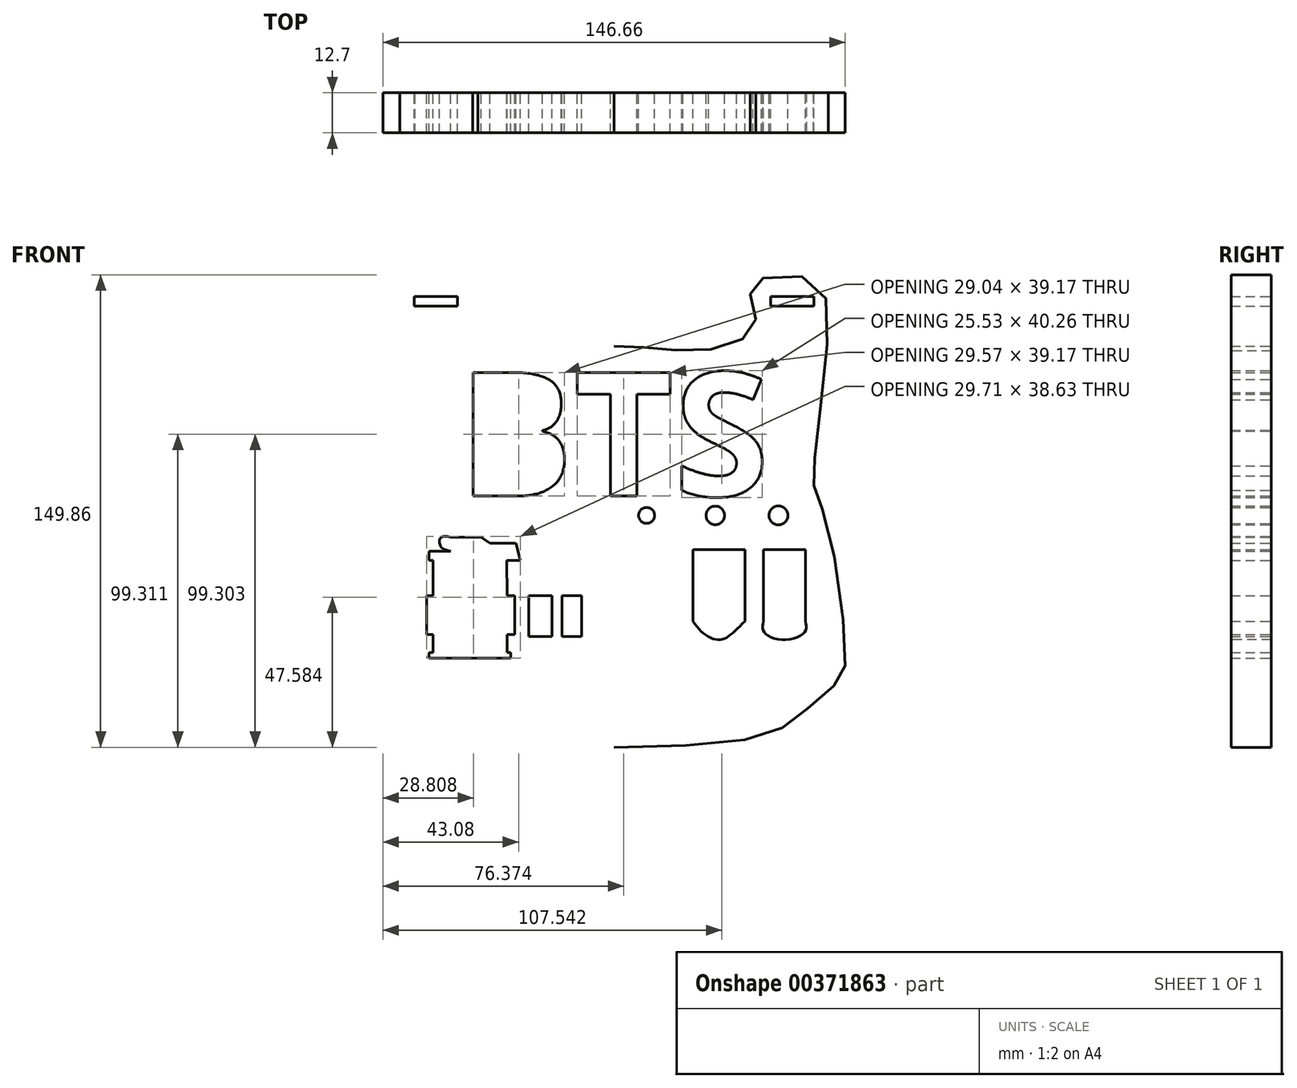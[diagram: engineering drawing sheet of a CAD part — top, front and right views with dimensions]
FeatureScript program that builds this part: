
annotation { "Feature Type Name" : "Feature", "Feature Type Description" : "" }
export const myFeature = defineFeature(function(context is Context, id is Id, definition is map)
    precondition{}
    {
        {
            var Q0;
            Q0=qCreatedBy(makeId("Front.planeOp"),FACE);
            var sketch = newSketch(context, id + "F0", { "sketchPlane" : qUnion([Q0])});
            skFitSpline(sketch, "E0", {"points": [v(0, 47.49) * mm, v(-11.8, 46.91) * mm, v(-26.2, 46.05) * mm, v(-40.87, 49.8) * mm, v(-44.9, 55.83) * mm, v(-43.17, 64.18) * mm, v(-45.76, 68.5) * mm, v(-63.32, 68.2) * mm, v(-67.63, 48.93) * mm, v(-63.32, 9.2) * mm, v(-63.6, 2.3) * mm, v(-67.92, -10.07) * mm, v(-73.32, -52.11) * mm, v(-70.96, -58.89) * mm, v(-59.95, -68.62) * mm, v(-48.35, -75.7) * mm, v(0, -79.72) * mm], "startDerivative": vector(-215.17, -5.96) * mm, "endDerivative": vector(548.69, -6.84) * mm});
            skFitSpline(sketch, "E1.MirrorCS", {"points": [v(0, 47.49) * mm, v(11.8, 46.91) * mm, v(26.2, 46.05) * mm, v(40.87, 49.8) * mm, v(44.9, 55.83) * mm, v(43.17, 64.18) * mm, v(45.76, 68.5) * mm, v(63.32, 68.2) * mm, v(67.63, 48.93) * mm, v(63.32, 9.2) * mm, v(63.6, 2.3) * mm, v(67.92, -10.07) * mm, v(73.32, -52.11) * mm, v(70.96, -58.89) * mm, v(59.95, -68.62) * mm, v(48.35, -75.7) * mm, v(0, -79.72) * mm], "startDerivative": vector(215.17, -5.96) * mm, "endDerivative": vector(-548.69, -6.84) * mm});
            skLineSegment(sketch, "E2", {"start": v(-58.71, -17.56) * mm, "end": v(-58.71, -20.44) * mm});
            skLineSegment(sketch, "E3", {"start": v(-58.71, -20.44) * mm, "end": v(-32.8, -20.44) * mm});
            skLineSegment(sketch, "E4", {"start": v(-32.8, -20.44) * mm, "end": v(-32.8, -17.56) * mm});
            skLineSegment(sketch, "E5", {"start": v(-32.8, -17.56) * mm, "end": v(-58.71, -17.56) * mm});
            skLineSegment(sketch, "E6", {"start": v(-57.44, -20.44) * mm, "end": v(-57.44, -31.6) * mm});
            skLineSegment(sketch, "E7", {"start": v(-57.44, -31.6) * mm, "end": v(-33.87, -31.6) * mm});
            skLineSegment(sketch, "E8", {"start": v(-34.07, -20.44) * mm, "end": v(-33.87, -31.6) * mm});
            skLineSegment(sketch, "E9", {"start": v(-57.44, -31.6) * mm, "end": v(-59.38, -31.6) * mm});
            skLineSegment(sketch, "E10", {"start": v(-59.38, -31.6) * mm, "end": v(-59.38, -44) * mm});
            skLineSegment(sketch, "E11", {"start": v(-59.38, -44) * mm, "end": v(-31.55, -44) * mm});
            skLineSegment(sketch, "E12", {"start": v(-31.55, -44) * mm, "end": v(-31.55, -31.6) * mm});
            skLineSegment(sketch, "E13", {"start": v(-31.55, -31.6) * mm, "end": v(-33.87, -31.6) * mm});
            skLineSegment(sketch, "E14", {"start": v(-57.44, -44) * mm, "end": v(-57.44, -49.66) * mm});
            skLineSegment(sketch, "E15", {"start": v(-57.44, -49.66) * mm, "end": v(-33.87, -49.66) * mm});
            skLineSegment(sketch, "E16", {"start": v(-33.87, -49.66) * mm, "end": v(-33.87, -44) * mm});
            skLineSegment(sketch, "E17", {"start": v(-57.44, -49.66) * mm, "end": v(-58.71, -49.66) * mm});
            skLineSegment(sketch, "E18", {"start": v(-58.71, -49.66) * mm, "end": v(-58.71, -51.45) * mm});
            skLineSegment(sketch, "E19", {"start": v(-58.71, -51.45) * mm, "end": v(-32.8, -51.45) * mm});
            skLineSegment(sketch, "E20", {"start": v(-32.8, -51.45) * mm, "end": v(-32.8, -49.66) * mm});
            skLineSegment(sketch, "E21", {"start": v(-32.8, -49.66) * mm, "end": v(-33.87, -49.66) * mm});
            skLineSegment(sketch, "E22", {"start": v(-51.85, -17.56) * mm, "end": v(-51.85, -13.04) * mm});
            skLineSegment(sketch, "E23", {"start": v(-51.85, -13.04) * mm, "end": v(-42.16, -13.04) * mm});
            skLineSegment(sketch, "E24", {"start": v(-42.16, -13.04) * mm, "end": v(-39.36, -15) * mm});
            skLineSegment(sketch, "E25", {"start": v(-39.36, -15) * mm, "end": v(-31.14, -15) * mm});
            skLineSegment(sketch, "E26", {"start": v(-31.14, -15) * mm, "end": v(-29.66, -20.44) * mm});
            skLineSegment(sketch, "E27", {"start": v(-29.66, -20.44) * mm, "end": v(-32.8, -20.44) * mm});
            skLineSegment(sketch, "E28", {"start": v(-51.85, -15.3) * mm, "end": v(-42.65, -15.3) * mm});
            skLineSegment(sketch, "E29", {"start": v(-42.65, -15.3) * mm, "end": v(-40.68, -17.56) * mm});
            skFitSpline(sketch, "E30", {"points": [v(-51.85, -17.56) * mm, v(-54.97, -16) * mm, v(-54.97, -13.2) * mm, v(-51.85, -13.04) * mm], "startDerivative": vector(-10.72, 2.62) * mm, "endDerivative": vector(11.36, -2.08) * mm});
            skLineSegment(sketch, "E31", {"start": v(-27.04, -31.6) * mm, "end": v(-27.04, -44.6) * mm});
            skLineSegment(sketch, "E32", {"start": v(-27.04, -44.6) * mm, "end": v(-19.64, -44.6) * mm});
            skLineSegment(sketch, "E33", {"start": v(-19.64, -44.6) * mm, "end": v(-19.64, -31.6) * mm});
            skLineSegment(sketch, "E34", {"start": v(-19.64, -31.6) * mm, "end": v(-27.04, -31.6) * mm});
            skLineSegment(sketch, "E35", {"start": v(-16.52, -31.6) * mm, "end": v(-16.52, -44.6) * mm});
            skLineSegment(sketch, "E36", {"start": v(-16.52, -44.6) * mm, "end": v(-10.27, -44.6) * mm});
            skLineSegment(sketch, "E37", {"start": v(-10.27, -44.6) * mm, "end": v(-10.27, -31.6) * mm});
            skLineSegment(sketch, "E38", {"start": v(-10.27, -31.6) * mm, "end": v(-16.52, -31.6) * mm});
            skLineSegment(sketch, "E39", {"start": v(25.03, -17.07) * mm, "end": v(41.52, -17.07) * mm});
            skLineSegment(sketch, "E40", {"start": v(41.52, -17.07) * mm, "end": v(41.52, -39.75) * mm});
            skLineSegment(sketch, "E41", {"start": v(25.03, -17.07) * mm, "end": v(25.03, -39.75) * mm});
            skFitSpline(sketch, "E42", {"points": [v(25.03, -39.75) * mm, v(33.27, -45.64) * mm, v(41.52, -39.75) * mm], "startDerivative": vector(12.72, -19.95) * mm, "endDerivative": vector(20.1, 19.1) * mm});
            skLineSegment(sketch, "E43", {"start": v(47.4, -17.07) * mm, "end": v(47.4, -39.75) * mm});
            skLineSegment(sketch, "E44", {"start": v(47.4, -39.75) * mm, "end": v(47.4, -17.07) * mm});
            skLineSegment(sketch, "E45", {"start": v(60.66, -17.07) * mm, "end": v(60.66, -39.75) * mm});
            skLineSegment(sketch, "E46", {"start": v(47.4, -17.07) * mm, "end": v(60.66, -17.07) * mm});
            skFitSpline(sketch, "E47", {"points": [v(47.4, -39.75) * mm, v(47.4, -42.93) * mm, v(53.6, -45.64) * mm, v(60.66, -42.93) * mm, v(60.66, -39.75) * mm], "startDerivative": vector(-4.18, -16.44) * mm, "endDerivative": vector(-4.64, 16.48) * mm});
            skCircle(sketch, "E48", {"center": v(33.57, -40.63) * mm, "radius": 1.67 * mm});
            skCircle(sketch, "E49", {"center": v(53.89, -42.1) * mm, "radius": 1.67 * mm});
            skCircle(sketch, "E50", {"center": v(10.3, -6.18) * mm, "radius": 2.53 * mm});
            skCircle(sketch, "E51", {"center": v(32.1, -6.18) * mm, "radius": 2.94 * mm});
            skCircle(sketch, "E52", {"center": v(52.12, -6.18) * mm, "radius": 3 * mm});
            skCircle(sketch, "E53", {"center": v(-53.57, -15.3) * mm, "radius": 0.8 * mm});
            skText(sketch, "E54", { "text": "BTS", "fontName": "OpenSans-Bold.ttf"});
            skLineSegment(sketch, "E55.bottom", {"start": v(-63.32, 63.28) * mm, "end": v(-49.7, 63.28) * mm});
            skLineSegment(sketch, "E55.top", {"start": v(-63.32, 60.18) * mm, "end": v(-49.7, 60.18) * mm});
            skLineSegment(sketch, "E55.left", {"start": v(-63.32, 63.28) * mm, "end": v(-63.32, 60.18) * mm});
            skLineSegment(sketch, "E55.right", {"start": v(-49.7, 63.28) * mm, "end": v(-49.7, 60.18) * mm});
            skLineSegment(sketch, "E56.MirrorCS", {"start": v(63.32, 60.18) * mm, "end": v(49.7, 60.18) * mm});
            skLineSegment(sketch, "E57.MirrorCS", {"start": v(63.32, 63.28) * mm, "end": v(49.7, 63.28) * mm});
            skLineSegment(sketch, "E58.MirrorCS", {"start": v(49.7, 63.28) * mm, "end": v(49.7, 60.18) * mm});
            skLineSegment(sketch, "E59.MirrorCS", {"start": v(63.32, 63.28) * mm, "end": v(63.32, 60.18) * mm});
            const initialGuessF0  = {"E54": [-0.0497, 0, 1, 0, 0.0395]};
            skSetInitialGuess(sketch, initialGuessF0);
            skSolve(sketch);
        }
        {
            var Q0;
            Q0 = qSketchRegion(id + "F0", true);
            extrude(context, id + "F1", {"entities" : qUnion([Q0]), "depth" : 12.7 * mm});
        }
    });
